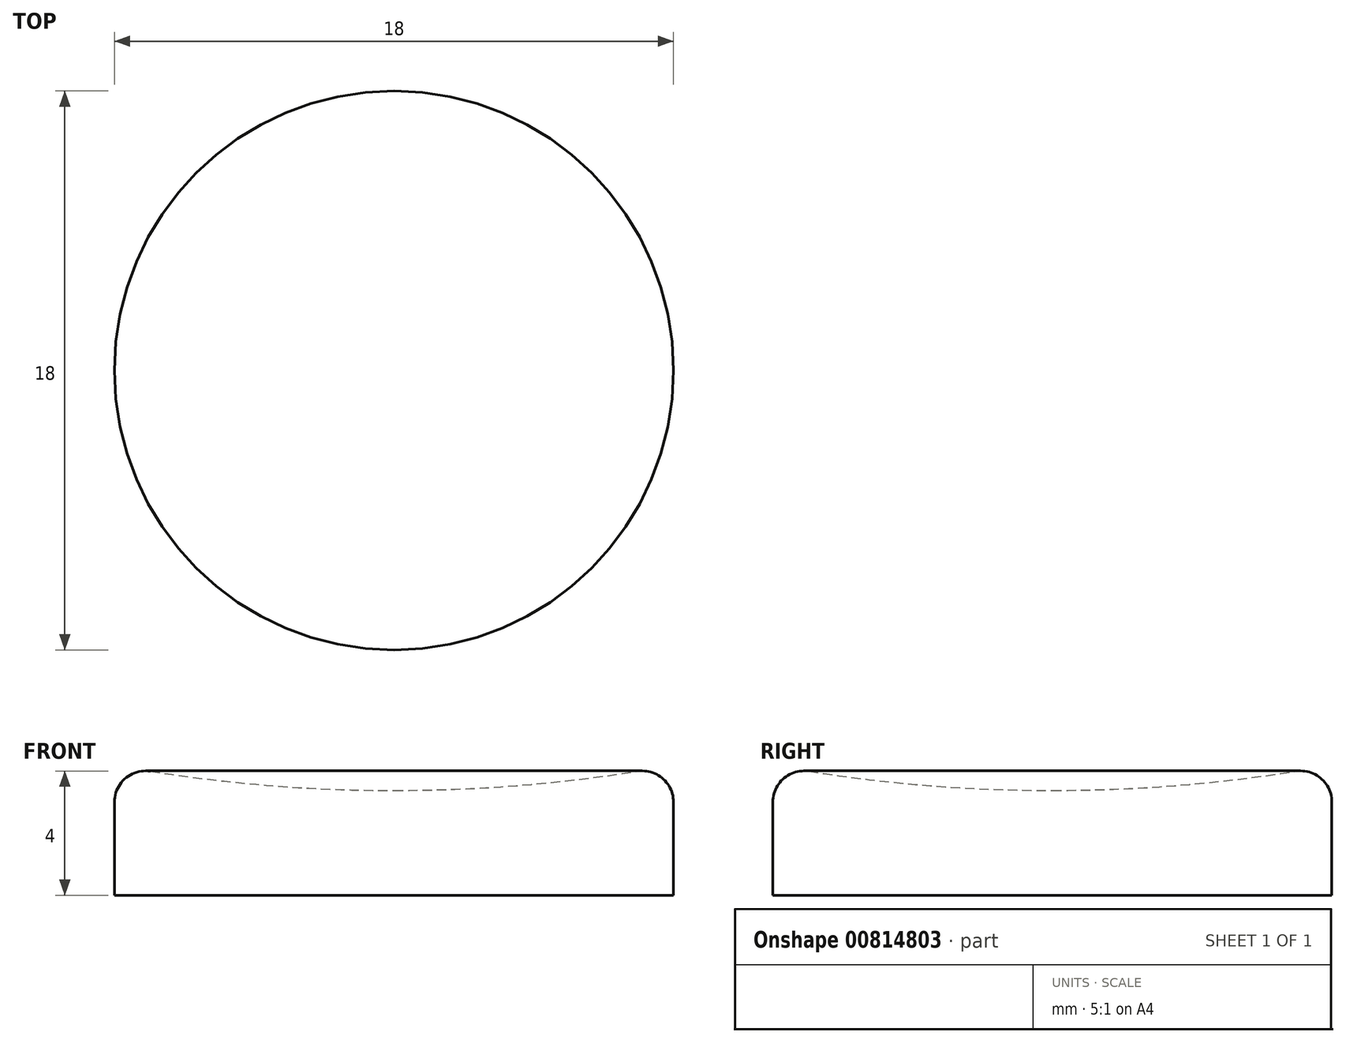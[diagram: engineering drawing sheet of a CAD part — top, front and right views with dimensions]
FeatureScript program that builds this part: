
annotation { "Feature Type Name" : "Feature", "Feature Type Description" : "" }
export const myFeature = defineFeature(function(context is Context, id is Id, definition is map)
    precondition{}
    {
        {
            var Q0;
            Q0=qCreatedBy(makeId("Front.planeOp"),FACE);
            var sketch = newSketch(context, id + "F0", { "sketchPlane" : qUnion([Q0])});
            skLineSegment(sketch, "E0", {"start": v(0, -15.1) * mm, "end": v(0, 24.15) * mm});
            skLineSegment(sketch, "E1", {"start": v(0, 0) * mm, "end": v(9, 0) * mm});
            skCircle(sketch, "E2", {"center": v(0, 53.37) * mm, "radius": 50 * mm});
            skCircle(sketch, "E3", {"center": v(8, 3) * mm, "radius": 1 * mm});
            skLineSegment(sketch, "E4", {"start": v(9, 3) * mm, "end": v(9, 0) * mm});
            skSolve(sketch);
        }
        {
            var Q0;
            {var subQ5=sQuery(id+"F0.wireOp",EDGE,"E1");Q0=makeQuery(id+"F0.imprint","IMPRINT",FACE,{"disambiguationData":[TD([[makeQuery(id+"F0.imprint","IMPRINT",EDGE,{"derivedFrom":subQ5}),1.0]])]});}
            var Q1;
            {var subQ0=sQuery(id+"F0.wireOp",EDGE,"E3");var subQ1=makeQuery(id+"F0.imprint","INTERSECT",VERTEX,{"derivedFrom":[subQ0,sQuery(id+"F0.wireOp",EDGE,"E4")]});Q1=makeQuery(id+"F0.imprint","IMPRINT",FACE,{"disambiguationData":[TD([[makeQuery(id+"F0.imprint","IMPRINT",EDGE,{"disambiguationData":[TD([[subQ1,-1.0]])],"derivedFrom":subQ0}),1.0]])]});}
            var Q2;
            Q2=sQuery(id+"F0.wireOp",EDGE,"E0");
            revolve(context, id + "F1", {"surfaceOperationType" : NewSurfaceOperationType.NEW, "entities" : qUnion([Q0, Q1]), "axis" : qUnion([Q2]), "revolveType" : RevolveType.FULL});
        }
    });
